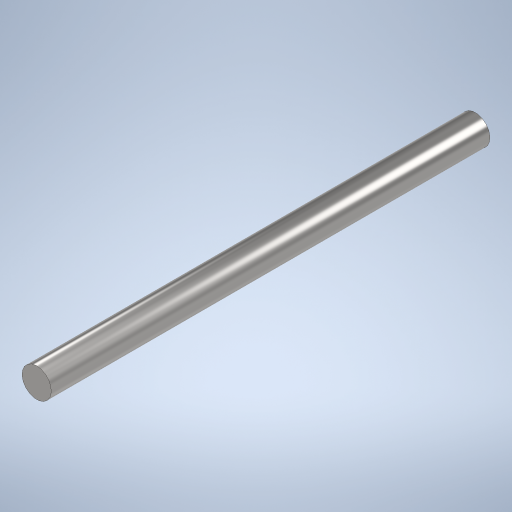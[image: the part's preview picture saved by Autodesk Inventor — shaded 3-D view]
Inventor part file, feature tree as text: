
AUTODESK INVENTOR PART (.ipt)
format: ipt  version: 2023 (Build 270158030, 158C)  size: 280,576 bytes
history: mixed  units: in
note: dims shown in document units (in); Inventor stores cm internally (conversion verified against a paired STEP export)
features: extrude x1, sketch x1, chamfer x1, imported_body x1
ambient origin geometry x8: Origin, YZ Plane, XZ Plane, XY Plane, X Axis, Y Axis, Z Axis, Center Point
bodies: Solid1 (imported_parasolid)
feature tree (4):
  extrude  "Extrusion1"  Depth=0.3937in TaperAngle=0.0deg
  sketch  "Sketch1"  dims[d0=5.9055in d1=0.3937in d2=0.0in]
  chamfer  "Chamfer1"  [1 undecoded]
  imported_body  NMx_Import_Brep_tag  [imported B-rep: ~3 faces, bbox_mm=[0.0, 10.0, 150.0]]
note: 1 required parameter value undecoded (feature->parameter linkage not recoverable at this tier; creation-order binding heuristic only, values carry confidence <= 0.55)
